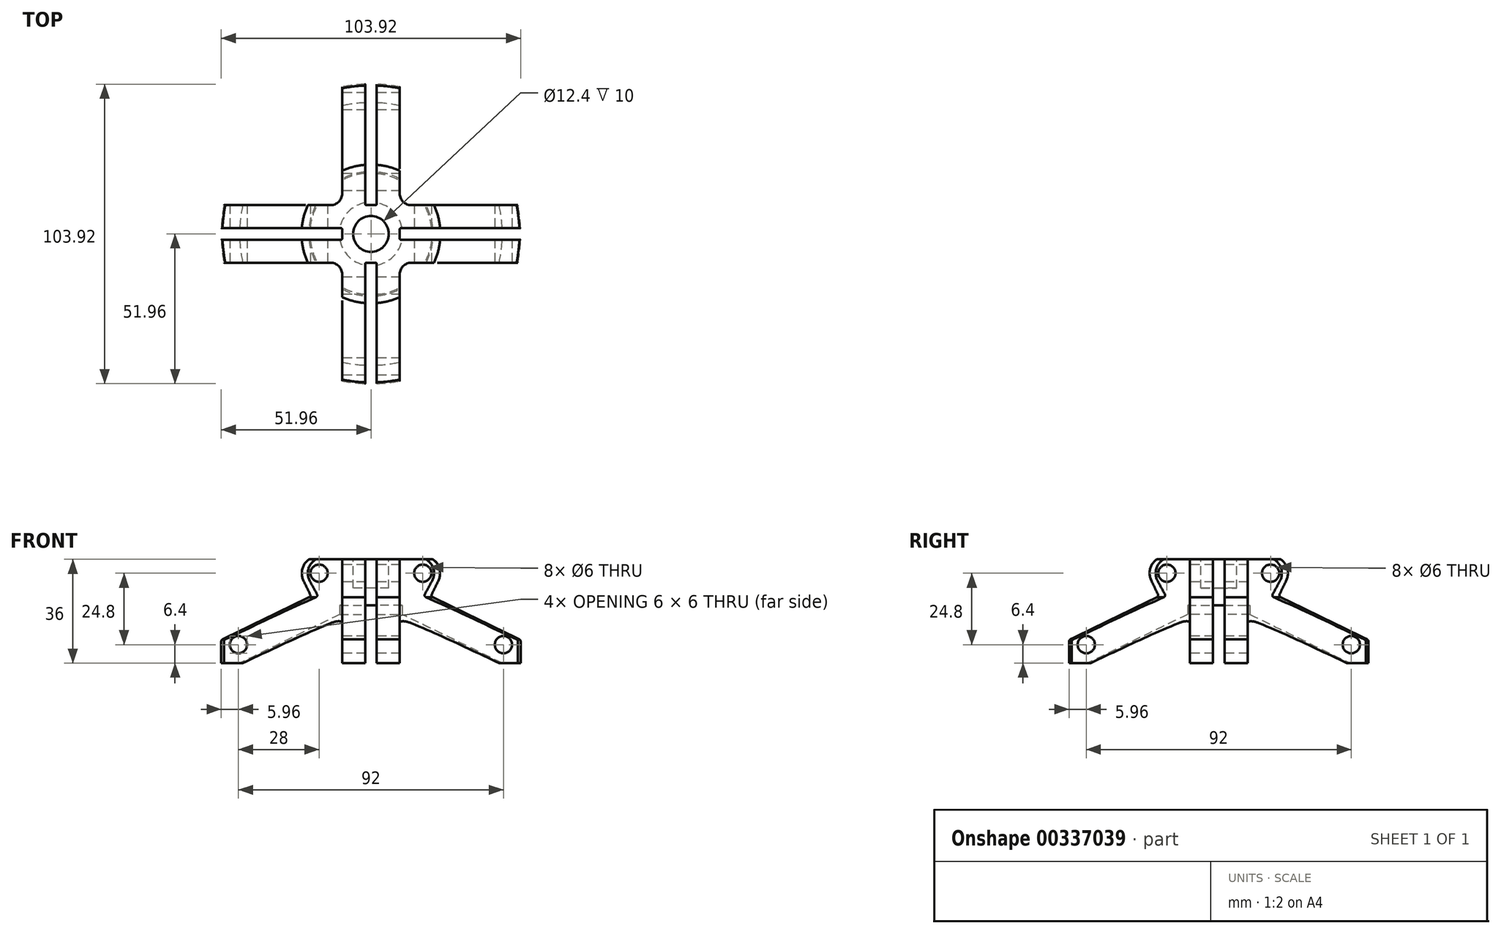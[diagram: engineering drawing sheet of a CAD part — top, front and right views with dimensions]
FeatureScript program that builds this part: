
annotation { "Feature Type Name" : "Feature", "Feature Type Description" : "" }
export const myFeature = defineFeature(function(context is Context, id is Id, definition is map)
    precondition{}
    {
        {
            var Q0;
            Q0=qCreatedBy(makeId("Top.planeOp"),FACE);
            var sketch = newSketch(context, id + "F0", { "sketchPlane" : qUnion([Q0])});
            skCircle(sketch, "E0", {"center": v(0, 0) * mm, "radius": 52 * mm});
            skSolve(sketch);
        }
        {
            var Q0;
            Q0=makeQuery(id+"F0.imprint","IMPRINT",FACE,{"disambiguationData":[TD([[makeQuery(id+"F0.imprint","IMPRINT",EDGE,{"derivedFrom":sQuery(id+"F0.wireOp",EDGE,"E0")}),1.0]])]});
            extrude(context, id + "F1", {"entities" : qUnion([Q0]), "depth" : 36 * mm});
        }
        {
            var Q0;
            Q0=makeQuery(id+"F1.opExtrude","CAP_FACE",FACE,{"disambiguationData":[OSD([sQuery(id+"F0.wireOp",EDGE,"E0")])],"isStart":true});
            var sketch = newSketch(context, id + "F2", { "sketchPlane" : qUnion([Q0])});
            skCircle(sketch, "E1", {"center": v(0, 0) * mm, "radius": 11 * mm});
            skSolve(sketch);
        }
        {
            var Q0;
            Q0=makeQuery(id+"F2.imprint","IMPRINT",FACE,{"disambiguationData":[TD([[makeQuery(id+"F2.imprint","IMPRINT",EDGE,{"derivedFrom":sQuery(id+"F2.wireOp",EDGE,"E1")}),1.0]])]});
            extrude(context, id + "F3", {"entities" : qUnion([Q0]), "operationType" : NewBodyOperationType.REMOVE, "oppositeDirection" : true, "depth" : 20 * mm});
        }
        {
            var Q0;
            Q0=makeQuery(id+"F1.opExtrude","CAP_FACE",FACE,{"disambiguationData":[OSD([sQuery(id+"F0.wireOp",EDGE,"E0")])],"isStart":true});
            var sketch = newSketch(context, id + "F4", { "sketchPlane" : qUnion([Q0])});
            skLineSegment(sketch, "E2", {"start": v(2, 10.4) * mm, "end": v(2, 60) * mm});
            skLineSegment(sketch, "E3", {"start": v(2, 60) * mm, "end": v(-2, 60) * mm});
            skLineSegment(sketch, "E4", {"start": v(-2, 60) * mm, "end": v(-2, 10.4) * mm});
            skLineSegment(sketch, "E5", {"start": v(-1.6, 10) * mm, "end": v(1.6, 10) * mm});
            skLineSegment(sketch, "E6", {"start": v(10.4, 2) * mm, "end": v(60, 2) * mm});
            skLineSegment(sketch, "E7", {"start": v(60, 2) * mm, "end": v(60, -2) * mm});
            skLineSegment(sketch, "E8", {"start": v(60, -2) * mm, "end": v(10.4, -2) * mm});
            skLineSegment(sketch, "E9", {"start": v(10, -1.6) * mm, "end": v(10, 1.6) * mm});
            skLineSegment(sketch, "E10", {"start": v(-2, -60) * mm, "end": v(-2, -10.4) * mm});
            skLineSegment(sketch, "E11", {"start": v(-1.6, -10) * mm, "end": v(1.6, -10) * mm});
            skLineSegment(sketch, "E12", {"start": v(2, -10.4) * mm, "end": v(2, -60) * mm});
            skLineSegment(sketch, "E13", {"start": v(2, -60) * mm, "end": v(-2, -60) * mm});
            skLineSegment(sketch, "E14", {"start": v(-60, 2) * mm, "end": v(-10.4, 2) * mm});
            skLineSegment(sketch, "E15", {"start": v(-10, 1.6) * mm, "end": v(-10, -1.6) * mm});
            skLineSegment(sketch, "E16", {"start": v(-10.4, -2) * mm, "end": v(-60, -2) * mm});
            skLineSegment(sketch, "E17", {"start": v(-60, -2) * mm, "end": v(-60, 2) * mm});
            skPoint(sketch, "E18", {"position": v(0, 10) * mm});
            skPoint(sketch, "E19.visualSharp", {"position": v(-2, 10) * mm});
            skArc(sketch, "E19.filletArc", {"start": v(-2, 10.4) * mm, "mid": v(-1.88, 10.12) * mm, "end": v(-1.6, 10) * mm});
            skPoint(sketch, "E20.visualSharp", {"position": v(2, 10) * mm});
            skArc(sketch, "E20.filletArc", {"start": v(1.6, 10) * mm, "mid": v(1.88, 10.12) * mm, "end": v(2, 10.4) * mm});
            skPoint(sketch, "E21", {"position": v(10, 0) * mm});
            skPoint(sketch, "E22.visualSharp", {"position": v(10, 2) * mm});
            skArc(sketch, "E22.filletArc", {"start": v(10.4, 2) * mm, "mid": v(10.12, 1.88) * mm, "end": v(10, 1.6) * mm});
            skPoint(sketch, "E23.visualSharp", {"position": v(10, -2) * mm});
            skArc(sketch, "E23.filletArc", {"start": v(10, -1.6) * mm, "mid": v(10.12, -1.88) * mm, "end": v(10.4, -2) * mm});
            skPoint(sketch, "E24", {"position": v(-10, 0) * mm});
            skPoint(sketch, "E25", {"position": v(0, -10) * mm});
            skPoint(sketch, "E26.visualSharp", {"position": v(2, -10) * mm});
            skArc(sketch, "E26.filletArc", {"start": v(2, -10.4) * mm, "mid": v(1.88, -10.12) * mm, "end": v(1.6, -10) * mm});
            skPoint(sketch, "E27.visualSharp", {"position": v(-2, -10) * mm});
            skArc(sketch, "E27.filletArc", {"start": v(-1.6, -10) * mm, "mid": v(-1.88, -10.12) * mm, "end": v(-2, -10.4) * mm});
            skPoint(sketch, "E28.visualSharp", {"position": v(-10, -2) * mm});
            skArc(sketch, "E28.filletArc", {"start": v(-10.4, -2) * mm, "mid": v(-10.12, -1.88) * mm, "end": v(-10, -1.6) * mm});
            skPoint(sketch, "E29.visualSharp", {"position": v(-10, 2) * mm});
            skArc(sketch, "E29.filletArc", {"start": v(-10, 1.6) * mm, "mid": v(-10.12, 1.88) * mm, "end": v(-10.4, 2) * mm});
            skSolve(sketch);
        }
        {
            var Q0;
            {var subQ0=sQuery(id+"F4.wireOp",EDGE,"E17");Q0=makeQuery(id+"F4.imprint","IMPRINT",FACE,{"disambiguationData":[TD([[makeQuery(id+"F4.imprint","IMPRINT",EDGE,{"derivedFrom":subQ0}),-1.0]])]});}
            var Q1;
            {var subQ0=sQuery(id+"F4.wireOp",EDGE,"E14");var subQ1=makeQuery(id+"F1.opExtrude","CAP_EDGE",EDGE,{"disambiguationData":[OSD([sQuery(id+"F0.wireOp",EDGE,"E0")])],"isStart":true});var subQ2=makeQuery(id+"F4.imprint","INTERSECT",VERTEX,{"derivedFrom":[subQ1,subQ0]});Q1=makeQuery(id+"F4.imprint","IMPRINT",FACE,{"disambiguationData":[TD([[makeQuery(id+"F4.imprint","IMPRINT",EDGE,{"disambiguationData":[TD([[subQ2,-1.0]])],"derivedFrom":subQ0}),-1.0]])]});}
            var Q2;
            Q2=makeQuery(id+"F4.imprint","IMPRINT",FACE,{"disambiguationData":[TD([[makeQuery(id+"F4.imprint","IMPRINT",EDGE,{"derivedFrom":sQuery(id+"F4.wireOp",EDGE,"E15")}),-1.0]])]});
            var Q3;
            Q3=makeQuery(id+"F4.imprint","IMPRINT",FACE,{"disambiguationData":[TD([[makeQuery(id+"F4.imprint","IMPRINT",EDGE,{"derivedFrom":sQuery(id+"F4.wireOp",EDGE,"E5")}),1.0]])]});
            var Q4;
            {var subQ0=sQuery(id+"F4.wireOp",EDGE,"E2");var subQ1=makeQuery(id+"F1.opExtrude","CAP_EDGE",EDGE,{"disambiguationData":[OSD([sQuery(id+"F0.wireOp",EDGE,"E0")])],"isStart":true});var subQ2=makeQuery(id+"F4.imprint","INTERSECT",VERTEX,{"derivedFrom":[subQ1,subQ0]});Q4=makeQuery(id+"F4.imprint","IMPRINT",FACE,{"disambiguationData":[TD([[makeQuery(id+"F4.imprint","IMPRINT",EDGE,{"disambiguationData":[TD([[subQ2,1.0]])],"derivedFrom":subQ0}),1.0]])]});}
            var Q5;
            {var subQ0=sQuery(id+"F4.wireOp",EDGE,"E3");Q5=makeQuery(id+"F4.imprint","IMPRINT",FACE,{"disambiguationData":[TD([[makeQuery(id+"F4.imprint","IMPRINT",EDGE,{"derivedFrom":subQ0}),1.0]])]});}
            var Q6;
            Q6=makeQuery(id+"F4.imprint","IMPRINT",FACE,{"disambiguationData":[TD([[makeQuery(id+"F4.imprint","IMPRINT",EDGE,{"derivedFrom":sQuery(id+"F4.wireOp",EDGE,"E9")}),-1.0]])]});
            var Q7;
            {var subQ0=sQuery(id+"F4.wireOp",EDGE,"E6");var subQ1=makeQuery(id+"F1.opExtrude","CAP_EDGE",EDGE,{"disambiguationData":[OSD([sQuery(id+"F0.wireOp",EDGE,"E0")])],"isStart":true});var subQ2=makeQuery(id+"F4.imprint","INTERSECT",VERTEX,{"derivedFrom":[subQ1,subQ0]});Q7=makeQuery(id+"F4.imprint","IMPRINT",FACE,{"disambiguationData":[TD([[makeQuery(id+"F4.imprint","IMPRINT",EDGE,{"disambiguationData":[TD([[subQ2,1.0]])],"derivedFrom":subQ0}),-1.0]])]});}
            var Q8;
            {var subQ0=sQuery(id+"F4.wireOp",EDGE,"E7");Q8=makeQuery(id+"F4.imprint","IMPRINT",FACE,{"disambiguationData":[TD([[makeQuery(id+"F4.imprint","IMPRINT",EDGE,{"derivedFrom":subQ0}),-1.0]])]});}
            var Q9;
            Q9=makeQuery(id+"F4.imprint","IMPRINT",FACE,{"disambiguationData":[TD([[makeQuery(id+"F4.imprint","IMPRINT",EDGE,{"derivedFrom":sQuery(id+"F4.wireOp",EDGE,"E11")}),-1.0]])]});
            var Q10;
            {var subQ0=sQuery(id+"F4.wireOp",EDGE,"E10");var subQ1=makeQuery(id+"F1.opExtrude","CAP_EDGE",EDGE,{"disambiguationData":[OSD([sQuery(id+"F0.wireOp",EDGE,"E0")])],"isStart":true});var subQ2=makeQuery(id+"F4.imprint","INTERSECT",VERTEX,{"derivedFrom":[subQ1,subQ0]});Q10=makeQuery(id+"F4.imprint","IMPRINT",FACE,{"disambiguationData":[TD([[makeQuery(id+"F4.imprint","IMPRINT",EDGE,{"disambiguationData":[TD([[subQ2,-1.0]])],"derivedFrom":subQ0}),-1.0]])]});}
            var Q11;
            {var subQ0=sQuery(id+"F4.wireOp",EDGE,"E13");Q11=makeQuery(id+"F4.imprint","IMPRINT",FACE,{"disambiguationData":[TD([[makeQuery(id+"F4.imprint","IMPRINT",EDGE,{"derivedFrom":subQ0}),-1.0]])]});}
            extrude(context, id + "F5", {"entities" : qUnion([Q0, Q1, Q2, Q3, Q4, Q5, Q6, Q7, Q8, Q9, Q10, Q11]), "operationType" : NewBodyOperationType.REMOVE, "endBound" : BoundingType.THROUGH_ALL, "oppositeDirection" : true, "depth" : 20 * mm});
        }
        {
            var Q0;
            Q0=makeQuery(id+"F5.boolean.opBoolean","COPY",FACE,{"derivedFrom":makeQuery(id+"F5.opExtrude","SWEPT_FACE",FACE,{"disambiguationData":[OSD([sQuery(id+"F4.wireOp",EDGE,"E4")])]})});
            var sketch = newSketch(context, id + "F6", { "sketchPlane" : qUnion([Q0])});
            skCircle(sketch, "E30", {"center": v(46, 6.4) * mm, "radius": 3 * mm});
            skCircle(sketch, "E31", {"center": v(-46, 6.4) * mm, "radius": 3 * mm});
            skCircle(sketch, "E32", {"center": v(18, 31.2) * mm, "radius": 3 * mm});
            skCircle(sketch, "E33", {"center": v(-18, 31.2) * mm, "radius": 3 * mm});
            skSolve(sketch);
        }
        {
            var Q0;
            Q0 = qSketchRegion(id + "F6", true);
            extrude(context, id + "F7", {"entities" : qUnion([Q0]), "operationType" : NewBodyOperationType.REMOVE, "endBound" : BoundingType.THROUGH_ALL, "depth" : 25 * mm, "hasSecondDirection" : true, "secondDirectionBound" : SecondDirectionBoundingType.THROUGH_ALL, "secondDirectionOppositeDirection" : true, "secondDirectionDepth" : 25 * mm});
        }
        {
            var Q0;
            Q0=makeQuery(id+"F5.boolean.opBoolean","COPY",FACE,{"derivedFrom":makeQuery(id+"F5.opExtrude","SWEPT_FACE",FACE,{"disambiguationData":[OSD([sQuery(id+"F4.wireOp",EDGE,"E6")])]})});
            var sketch = newSketch(context, id + "F8", { "sketchPlane" : qUnion([Q0])});
            skCircle(sketch, "E34", {"center": v(46, 6.4) * mm, "radius": 3 * mm});
            skCircle(sketch, "E35", {"center": v(-46, 6.4) * mm, "radius": 3 * mm});
            skCircle(sketch, "E36", {"center": v(18, 31.2) * mm, "radius": 3 * mm});
            skCircle(sketch, "E37", {"center": v(-18, 31.2) * mm, "radius": 3 * mm});
            skSolve(sketch);
        }
        {
            var Q0;
            Q0 = qSketchRegion(id + "F8", true);
            extrude(context, id + "F9", {"entities" : qUnion([Q0]), "operationType" : NewBodyOperationType.REMOVE, "endBound" : BoundingType.THROUGH_ALL, "depth" : 25 * mm, "hasSecondDirection" : true, "secondDirectionBound" : SecondDirectionBoundingType.THROUGH_ALL, "secondDirectionOppositeDirection" : true, "secondDirectionDepth" : 25 * mm});
        }
        {
            var Q0;
            Q0=makeQuery(id+"F1.opExtrude","CAP_FACE",FACE,{"disambiguationData":[OSD([sQuery(id+"F0.wireOp",EDGE,"E0")])],"isStart":false});
            var sketch = newSketch(context, id + "F10", { "sketchPlane" : qUnion([Q0])});
            skCircle(sketch, "E38", {"center": v(0, 0) * mm, "radius": 6.2 * mm});
            skSolve(sketch);
        }
        {
            var Q0;
            Q0=makeQuery(id+"F5.boolean.opBoolean","COPY",FACE,{"derivedFrom":makeQuery(id+"F5.opExtrude","SWEPT_FACE",FACE,{"disambiguationData":[OSD([sQuery(id+"F4.wireOp",EDGE,"E8")])]})});
            var sketch = newSketch(context, id + "F11", { "sketchPlane" : qUnion([Q0])});
            skCircle(sketch, "E39", {"center": v(18, 31.2) * mm, "radius": 6 * mm, "construction": true});
            skLineSegment(sketch, "E40", {"start": v(15.37, 25.8) * mm, "end": v(51.96, 8) * mm, "construction": true});
            skLineSegment(sketch, "E41", {"start": v(23.4, 28.57) * mm, "end": v(20.77, 23.18) * mm, "construction": true});
            skArc(sketch, "E42", {"start": v(21.83, 35.82) * mm, "mid": v(23.87, 32.46) * mm, "end": v(23.4, 28.57) * mm});
            skLineSegment(sketch, "E43", {"start": v(23.4, 28.57) * mm, "end": v(21.12, 23.9) * mm});
            skLineSegment(sketch, "E44", {"start": v(51.51, 8.22) * mm, "end": v(21.49, 22.83) * mm});
            skPoint(sketch, "E45.visualSharp", {"position": v(20.77, 23.18) * mm});
            skArc(sketch, "E45.filletArc", {"start": v(21.12, 23.9) * mm, "mid": v(21.08, 23.29) * mm, "end": v(21.49, 22.83) * mm});
            skLineSegment(sketch, "E46", {"start": v(51.96, 7.5) * mm, "end": v(51.96, 0) * mm, "construction": true});
            skArc(sketch, "E47.filletArc", {"start": v(51.96, 7.5) * mm, "mid": v(51.84, 7.92) * mm, "end": v(51.51, 8.22) * mm});
            skLineSegment(sketch, "E48", {"start": v(51.96, 36) * mm, "end": v(51.96, 7.5) * mm});
            skLineSegment(sketch, "E49", {"start": v(0.17, 36) * mm, "end": v(21.32, 36) * mm, "construction": true});
            skPoint(sketch, "E50.visualSharp", {"position": v(21.6, 36) * mm});
            skArc(sketch, "E50.filletArc", {"start": v(21.83, 35.82) * mm, "mid": v(21.6, 35.95) * mm, "end": v(21.32, 36) * mm});
            skLineSegment(sketch, "E51", {"start": v(21.32, 36) * mm, "end": v(51.96, 36) * mm});
            skLineSegment(sketch, "E52", {"start": v(10.82, 16.9) * mm, "end": v(10.82, 0) * mm});
            skLineSegment(sketch, "E53", {"start": v(10.82, 0) * mm, "end": v(45.55, 0) * mm});
            skLineSegment(sketch, "E54", {"start": v(45.55, 0) * mm, "end": v(10.82, 16.9) * mm});
            skSolve(sketch);
        }
        {
            var Q0;
            Q0 = qSketchRegion(id + "F11", true);
            var Q1;
            {var subQ0=sQuery(id+"F0.wireOp",EDGE,"E0");Q1=makeQuery(id+"F5.boolean.opBoolean","SPLIT",EDGE,{"disambiguationData":[TD([makeQuery(id+"F5.opExtrude","SWEPT_FACE",FACE,{"disambiguationData":[OSD([sQuery(id+"F4.wireOp",EDGE,"E8")])]})])],"derivedFrom":makeQuery(id+"F1.opExtrude","CAP_EDGE",EDGE,{"disambiguationData":[OSD([subQ0])],"isStart":false})});}
            revolve(context, id + "F12", {"operationType" : NewBodyOperationType.REMOVE, "entities" : qUnion([Q0]), "axis" : qUnion([Q1]), "revolveType" : RevolveType.FULL, "oppositeDirection" : true});
        }
        {
            var Q0;
            Q0=makeQuery(id+"F2.imprint","IMPRINT",FACE,{"disambiguationData":[TD([[makeQuery(id+"F2.imprint","IMPRINT",EDGE,{"derivedFrom":sQuery(id+"F2.wireOp",EDGE,"E1")}),-1.0]])]});
            var sketch = newSketch(context, id + "F13", { "sketchPlane" : qUnion([Q0])});
            skLineSegment(sketch, "E55", {"start": v(-10, 60) * mm, "end": v(-10, 14) * mm});
            skLineSegment(sketch, "E56", {"start": v(-14, 10) * mm, "end": v(-60, 10) * mm});
            skArc(sketch, "E57", {"start": v(-10, 60) * mm, "mid": v(-43.01, 43.01) * mm, "end": v(-60, 10) * mm});
            skPoint(sketch, "E58.visualSharp", {"position": v(-10, 10) * mm});
            skArc(sketch, "E58.filletArc", {"start": v(-14, 10) * mm, "mid": v(-11.17, 11.17) * mm, "end": v(-10, 14) * mm});
            skLineSegment(sketch, "E59.1.0", {"start": v(-10, -14) * mm, "end": v(-10, -60) * mm});
            skArc(sketch, "E59.1.1", {"start": v(-60, -10) * mm, "mid": v(-43.01, -43.01) * mm, "end": v(-10, -60) * mm});
            skArc(sketch, "E59.1.2", {"start": v(-10, -14) * mm, "mid": v(-11.17, -11.17) * mm, "end": v(-14, -10) * mm});
            skLineSegment(sketch, "E59.1.3", {"start": v(-60, -10) * mm, "end": v(-14, -10) * mm});
            skLineSegment(sketch, "E59.2.0", {"start": v(14, -10) * mm, "end": v(60, -10) * mm});
            skArc(sketch, "E59.2.1", {"start": v(10, -60) * mm, "mid": v(43.01, -43.01) * mm, "end": v(60, -10) * mm});
            skArc(sketch, "E59.2.2", {"start": v(14, -10) * mm, "mid": v(11.17, -11.17) * mm, "end": v(10, -14) * mm});
            skLineSegment(sketch, "E59.2.3", {"start": v(10, -60) * mm, "end": v(10, -14) * mm});
            skLineSegment(sketch, "E59.3.0", {"start": v(10, 14) * mm, "end": v(10, 60) * mm});
            skArc(sketch, "E59.3.1", {"start": v(60, 10) * mm, "mid": v(43.01, 43.01) * mm, "end": v(10, 60) * mm});
            skArc(sketch, "E59.3.2", {"start": v(10, 14) * mm, "mid": v(11.17, 11.17) * mm, "end": v(14, 10) * mm});
            skLineSegment(sketch, "E59.3.3", {"start": v(60, 10) * mm, "end": v(14, 10) * mm});
            skSolve(sketch);
        }
        {
            var Q0;
            Q0 = qSketchRegion(id + "F13", true);
            extrude(context, id + "F14", {"entities" : qUnion([Q0]), "operationType" : NewBodyOperationType.REMOVE, "endBound" : BoundingType.THROUGH_ALL, "oppositeDirection" : true, "depth" : 25 * mm});
        }
        {
            var Q0;
            Q0 = qSketchRegion(id + "F10", true);
            extrude(context, id + "F15", {"entities" : qUnion([Q0]), "operationType" : NewBodyOperationType.REMOVE, "oppositeDirection" : true, "depth" : 10 * mm});
        }
    });
